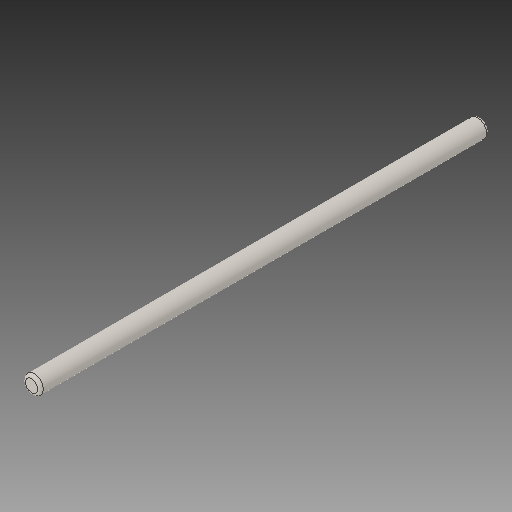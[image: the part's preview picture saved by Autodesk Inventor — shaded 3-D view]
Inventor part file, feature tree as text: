
AUTODESK INVENTOR PART (.ipt)
format: ipt  version: 2018 (Build 220112000, 112)  size: 83,456 bytes
history: native  units: in
note: dims shown in document units (in); Inventor stores cm internally (conversion verified against a paired STEP export)
features: fillet x1
ambient origin geometry x8: Origin, YZ Plane, XZ Plane, XY Plane, X Axis, Y Axis, Z Axis, Center Point
bodies: Solid1 (feature_tree)
feature tree (1):
  fillet  "Fillet1"  [1 undecoded]
note: 1 required parameter value undecoded (feature->parameter linkage not recoverable at this tier; creation-order binding heuristic only, values carry confidence <= 0.55)
